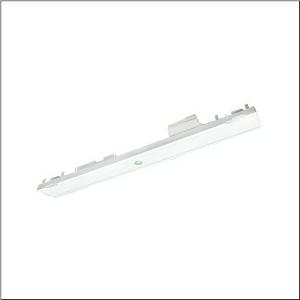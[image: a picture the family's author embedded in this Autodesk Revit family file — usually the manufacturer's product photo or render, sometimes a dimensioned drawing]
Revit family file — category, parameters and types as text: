
# Revit family: licross_r_56tl117c4x31_6d2f
name_source: partatom
category: Lighting Fixtures
units: mm (PartAtom-declared; Revit-internal decimal feet)

## family parameters
Cut with Voids When Loaded = No
Host = Face
Light Source = No
Part Type = Normal
Room Calculation Point = No
Round Connector Dimension = Use Diameter
Shared = No

## types (1)
- Licross® (1 x LED, 310 lm, 3.9 W, 4000K)
    Apparent Load = 4 VA
    CIE Flux Codes = 84 95 98 100 100
    Color Rendering = 70
    Color Temperature = 4000K
    Default Elevation = 1800 mm
    Description = Licross®, luminaire insert, of sheet steel, coil coated, white, length: 500mm, width: 59mm, height: 60mm, mounting height: 7..17m, emergency light element,LED rated luminous flux: 310lm, light colour: 740, control gear: CEAG, with plug, 6-pole, with phase selection, mains connection: 220..240V, AC/DC, 0/50..60Hz, rated input power: 3.9W, halogen-free wiring, for trunking rail, 9..14-core, for emergency light function, supply monitoring module CEAG, with address switch, choice between two emergency light lines via tool-free moving of contact pin prior to installation in trunking rail, primary light control with lens, of PMMA, primary optical cover: cover, of PMMA, light emission: direct distribution, primary light characteristic: symmetric,  for area, compatible with all CEAG STAR technology systems (ZB-S, DG-S (DualGuard-S), LP-STAR, AT-S+), protection rating (complete): IP40, insulation class (complete): insulation class I (protective earthing), certification: CE, UKCA, protection symbol: D if used in an environment without relevant dust loads, impact resistance: IK06, permissible ambient temperature for indoor applications: -20..+40°C, packaging unit: 1 piece
    Height = 60 mm  [stored 0.19685 ft]
    Lamp = 1 x LED
    Lamp Light Flux = 310 lm
    Lamp Power = 3.9 W
    Lamp count = 1
    Length = 500 mm  [stored 1.64042 ft]
    Luminous efficacy = 79 lm/W
    Manufacturer = Siteco
    ModVariant = No
    Model = 56TL117C4X31
    Mounting Place = Ceiling
    Mounting Type = Pendant
    Number of Poles = 1
    OnlyDefault = Yes
    Power Factor = 1
    Product Name = Licross®
    Product group = luminaire insert
    ProductGroupID = 902
    Protection Class = Protection class I
    Protection Degree = IP 40
    RLX_Detail_Level = 1
    RLX_Emergency_Light_Flux = 0 lm
    RLX_Emergency_Type = 0
    RLX_Emergency_Type_DB = No
    RlxData = <blob elided: 17833 chars, md5=72025084>
    Socket = socket
    Standby Power = 0 W
    System Light Flux = 310 lm
    System Power = 4 W
    Type Comments = Product without accessories
    Type Image = l_1251804.jpg
    URL = http://relux.com
    VarID = ---
    Voltage = 0 V
    Weight = 0.00 kg
    Width = 59 mm

note: [stored X ft] marks values corroborated as IEEE doubles in the binary element streams (Revit-internal decimal feet)

## geometry (parser evidence)
native form markers: Blend x4, Sweep x10
no freeform markers — native parametric forms only
